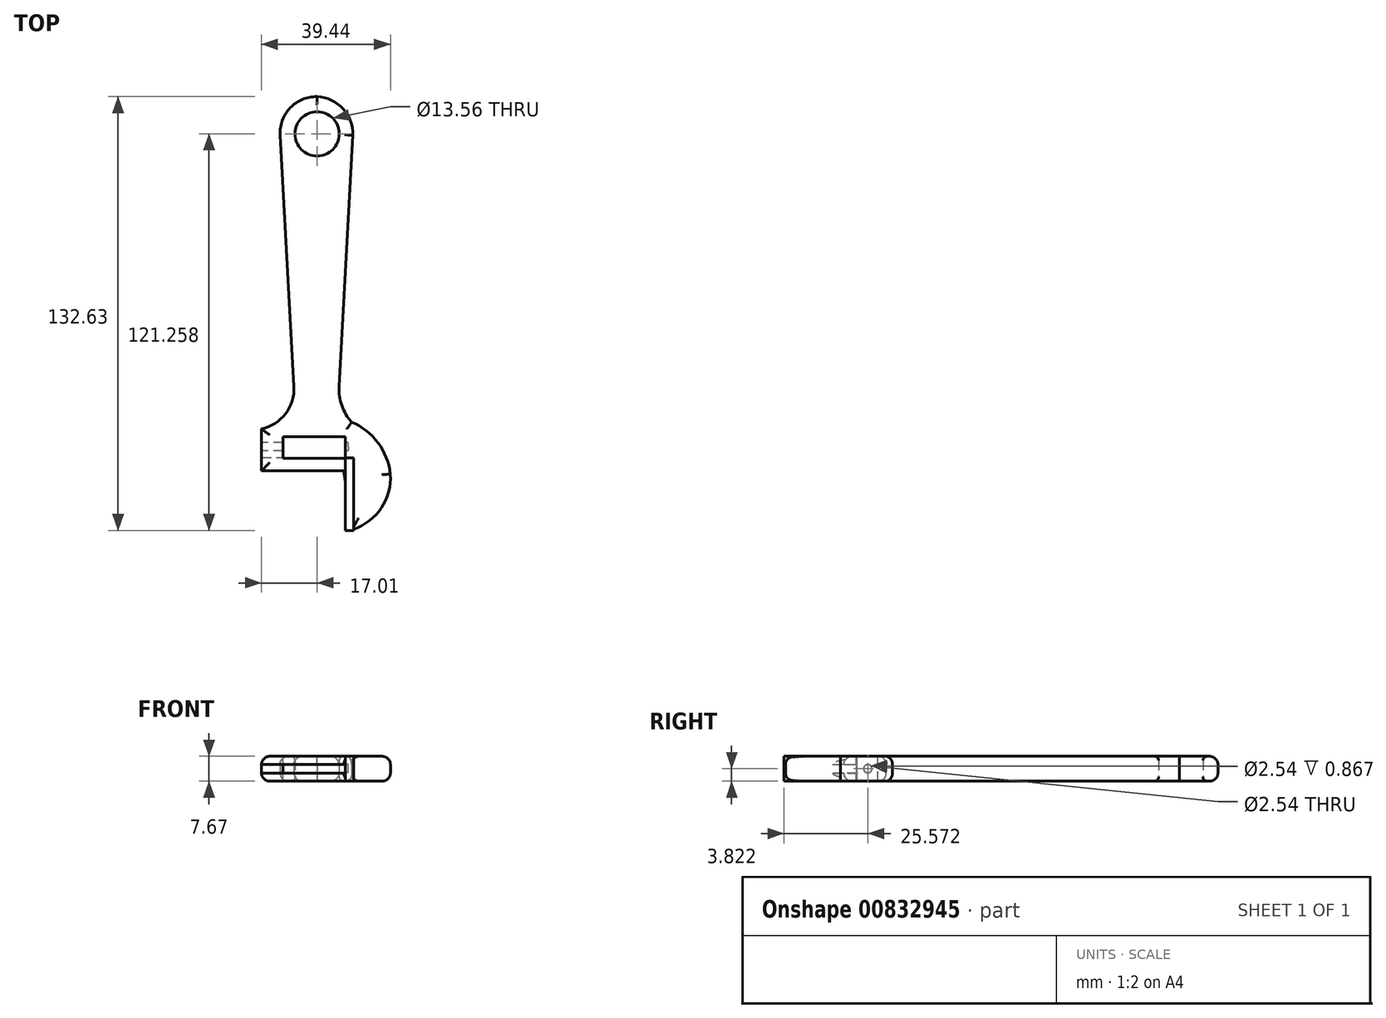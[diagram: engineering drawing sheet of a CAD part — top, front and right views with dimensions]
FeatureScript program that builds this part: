
annotation { "Feature Type Name" : "Feature", "Feature Type Description" : "" }
export const myFeature = defineFeature(function(context is Context, id is Id, definition is map)
    precondition{}
    {
        {
            var Q0;
            Q0=qCreatedBy(makeId("Top.planeOp"),FACE);
            var sketch = newSketch(context, id + "F0", { "sketchPlane" : qUnion([Q0])});
            skLineSegment(sketch, "E0", {"start": v(-7.08, -20.7) * mm, "end": v(-11.31, 56.2) * mm});
            skArc(sketch, "E1", {"start": v(0, 67.96) * mm, "mid": v(-8.22, 64.54) * mm, "end": v(-11.31, 56.2) * mm});
            skArc(sketch, "E2", {"start": v(10.94, 56.2) * mm, "mid": v(7.89, 64.32) * mm, "end": v(0, 67.96) * mm});
            skLineSegment(sketch, "E3", {"start": v(10.94, 56.2) * mm, "end": v(6.71, -20.7) * mm});
            skArc(sketch, "E4", {"start": v(6.71, -20.7) * mm, "mid": v(7.55, -26.5) * mm, "end": v(10.58, -31.54) * mm});
            skArc(sketch, "E5", {"start": v(22.39, -47.4) * mm, "mid": v(18.64, -37.87) * mm, "end": v(10.58, -31.54) * mm});
            skArc(sketch, "E6", {"start": v(10.58, -64.47) * mm, "mid": v(19.5, -58.03) * mm, "end": v(22.39, -47.4) * mm});
            skLineSegment(sketch, "E7", {"start": v(10.58, -64.47) * mm, "end": v(8.18, -46.44) * mm});
            skLineSegment(sketch, "E8", {"start": v(8.18, -46.44) * mm, "end": v(-17.01, -46.44) * mm});
            skLineSegment(sketch, "E9", {"start": v(-17.01, -46.44) * mm, "end": v(-17.01, -33.57) * mm});
            skArc(sketch, "E10", {"start": v(-17.01, -33.57) * mm, "mid": v(-9.65, -28.98) * mm, "end": v(-7.08, -20.7) * mm});
            skSolve(sketch);
        }
        {
            var Q0;
            Q0=makeQuery(id+"F0.imprint","IMPRINT",FACE,{"disambiguationData":[TD([[makeQuery(id+"F0.imprint","IMPRINT",EDGE,{"derivedFrom":sQuery(id+"F0.wireOp",EDGE,"E0")}),-1.0]])]});
            extrude(context, id + "F1", {"entities" : qUnion([Q0]), "depth" : 7.62 * mm, "offsetDistance" : 25.4 * mm});
        }
        {
            var Q0;
            Q0=makeQuery(id+"F1.opExtrude","CAP_FACE",FACE,{"disambiguationData":[OSD([sQuery(id+"F0.wireOp",EDGE,"E0"),sQuery(id+"F0.wireOp",EDGE,"E1"),sQuery(id+"F0.wireOp",EDGE,"E2"),sQuery(id+"F0.wireOp",EDGE,"E3"),sQuery(id+"F0.wireOp",EDGE,"E4"),sQuery(id+"F0.wireOp",EDGE,"E5"),sQuery(id+"F0.wireOp",EDGE,"E6"),sQuery(id+"F0.wireOp",EDGE,"E7"),sQuery(id+"F0.wireOp",EDGE,"E8"),sQuery(id+"F0.wireOp",EDGE,"E9"),sQuery(id+"F0.wireOp",EDGE,"E10")])],"isStart":true});
            fillet(context, id + "F2", {"entities" : qUnion([Q0]), "radius" : 2.54 * mm, "tangentPropagation" : true, "allowEdgeOverflow" : false});
        }
        {
            var Q0;
            Q0=makeQuery(id+"F1.opExtrude","CAP_FACE",FACE,{"disambiguationData":[OSD([sQuery(id+"F0.wireOp",EDGE,"E0"),sQuery(id+"F0.wireOp",EDGE,"E1"),sQuery(id+"F0.wireOp",EDGE,"E2"),sQuery(id+"F0.wireOp",EDGE,"E3"),sQuery(id+"F0.wireOp",EDGE,"E4"),sQuery(id+"F0.wireOp",EDGE,"E5"),sQuery(id+"F0.wireOp",EDGE,"E6"),sQuery(id+"F0.wireOp",EDGE,"E7"),sQuery(id+"F0.wireOp",EDGE,"E8"),sQuery(id+"F0.wireOp",EDGE,"E9"),sQuery(id+"F0.wireOp",EDGE,"E10")])],"isStart":false});
            fillet(context, id + "F3", {"entities" : qUnion([Q0]), "radius" : 2.54 * mm, "tangentPropagation" : true, "allowEdgeOverflow" : false});
        }
        {
            var Q0;
            Q0=qCreatedBy(makeId("Top.planeOp"),FACE);
            var sketch = newSketch(context, id + "F4", { "sketchPlane" : qUnion([Q0])});
            skLineSegment(sketch, "E11.bottom", {"start": v(-10.37, -35.97) * mm, "end": v(8.66, -35.97) * mm});
            skLineSegment(sketch, "E11.top", {"start": v(-10.37, -42.57) * mm, "end": v(8.66, -42.57) * mm});
            skLineSegment(sketch, "E11.left", {"start": v(-10.37, -35.97) * mm, "end": v(-10.37, -42.57) * mm});
            skLineSegment(sketch, "E11.right", {"start": v(8.66, -35.97) * mm, "end": v(8.66, -42.57) * mm});
            skSolve(sketch);
        }
        {
            var Q0;
            Q0 = qSketchRegion(id + "F4", true);
            extrude(context, id + "F5", {"entities" : qUnion([Q0]), "operationType" : NewBodyOperationType.REMOVE, "endBound" : BoundingType.SYMMETRIC, "oppositeDirection" : true, "depth" : 25.4 * mm, "offsetDistance" : 25.4 * mm});
        }
        {
            var Q0;
            Q0=qCreatedBy(makeId("Front.planeOp"),FACE);
            cPlane(context, id + "F6", {"entities" : qUnion([Q0]), "cplaneType" : CPlaneType.OFFSET, "offset" : 42.42 * mm, "width" : 152.4 * mm, "height" : 152.4 * mm});
        }
        {
            var Q0;
            Q0=qCreatedBy(id+"F6.planeOp",FACE);
            var sketch = newSketch(context, id + "F7", { "sketchPlane" : qUnion([Q0])});
            skLineSegment(sketch, "E12.bottom", {"start": v(-17.51, 5.16) * mm, "end": v(8.81, 5.16) * mm});
            skLineSegment(sketch, "E12.top", {"start": v(-17.51, 2.45) * mm, "end": v(8.81, 2.45) * mm});
            skLineSegment(sketch, "E12.left", {"start": v(-17.51, 5.16) * mm, "end": v(-17.51, 2.45) * mm});
            skLineSegment(sketch, "E12.right", {"start": v(8.81, 5.16) * mm, "end": v(8.81, 2.45) * mm});
            skSolve(sketch);
        }
        {
            var Q0;
            Q0 = qSketchRegion(id + "F7", true);
            extrude(context, id + "F8", {"entities" : qUnion([Q0]), "operationType" : NewBodyOperationType.REMOVE, "depth" : 25.4 * mm, "offsetDistance" : 25.4 * mm});
        }
        {
            var Q0;
            Q0=qCreatedBy(makeId("Right.planeOp"),FACE);
            cPlane(context, id + "F9", {"entities" : qUnion([Q0]), "cplaneType" : CPlaneType.OFFSET, "offset" : 12.7 * mm, "oppositeDirection" : true, "width" : 152.4 * mm, "height" : 152.4 * mm});
        }
        {
            var Q0;
            Q0=qCreatedBy(id+"F9.planeOp",FACE);
            var sketch = newSketch(context, id + "F10", { "sketchPlane" : qUnion([Q0])});
            skCircle(sketch, "E13", {"center": v(-39.1, 3.82) * mm, "radius": 1.27 * mm});
            skLineSegment(sketch, "E14", {"start": v(-39.1, 3.82) * mm, "end": v(-39.1, 5.1) * mm});
            skSolve(sketch);
        }
        {
            var Q0;
            Q0 = qSketchRegion(id + "F10", true);
            extrude(context, id + "F11", {"entities" : qUnion([Q0]), "operationType" : NewBodyOperationType.REMOVE, "endBound" : BoundingType.SYMMETRIC, "depth" : 44.45 * mm, "offsetDistance" : 25.4 * mm});
        }
        {
            var Q0;
            Q0=qCreatedBy(makeId("Right.planeOp"),FACE);
            cPlane(context, id + "F12", {"entities" : qUnion([Q0]), "cplaneType" : CPlaneType.OFFSET, "offset" : 8.64 * mm, "width" : 152.4 * mm, "height" : 152.4 * mm});
        }
        {
            var Q0;
            Q0=qCreatedBy(id+"F12.planeOp",FACE);
            var sketch = newSketch(context, id + "F13", { "sketchPlane" : qUnion([Q0])});
            skLineSegment(sketch, "E15.bottom", {"start": v(-42.5, 7.67) * mm, "end": v(-64.67, 7.67) * mm});
            skLineSegment(sketch, "E15.top", {"start": v(-42.5, 0) * mm, "end": v(-64.67, 0) * mm});
            skLineSegment(sketch, "E15.left", {"start": v(-42.5, 7.67) * mm, "end": v(-42.5, 0) * mm});
            skLineSegment(sketch, "E15.right", {"start": v(-64.67, 7.67) * mm, "end": v(-64.67, 0) * mm});
            skSolve(sketch);
        }
        {
            var Q0;
            Q0 = qSketchRegion(id + "F13", true);
            extrude(context, id + "F14", {"entities" : qUnion([Q0]), "operationType" : NewBodyOperationType.ADD, "depth" : 2.54 * mm, "offsetDistance" : 25.4 * mm});
        }
        {
            var Q0;
            Q0=qCreatedBy(makeId("Top.planeOp"),FACE);
            var sketch = newSketch(context, id + "F15", { "sketchPlane" : qUnion([Q0])});
            skCircle(sketch, "E16", {"center": v(0, 56.59) * mm, "radius": 6.78 * mm});
            skSolve(sketch);
        }
        {
            var Q0;
            Q0 = qSketchRegion(id + "F15", true);
            extrude(context, id + "F16", {"entities" : qUnion([Q0]), "operationType" : NewBodyOperationType.REMOVE, "endBound" : BoundingType.SYMMETRIC, "depth" : 25.4 * mm, "offsetDistance" : 25.4 * mm});
        }
        {
            var Q0;
            Q0=makeQuery(id+"F16.boolean.opBoolean","INTERSECT",EDGE,{"derivedFrom":[makeQuery(id+"F1.opExtrude","CAP_FACE",FACE,{"disambiguationData":[OSD([sQuery(id+"F0.wireOp",EDGE,"E0"),sQuery(id+"F0.wireOp",EDGE,"E1"),sQuery(id+"F0.wireOp",EDGE,"E2"),sQuery(id+"F0.wireOp",EDGE,"E3"),sQuery(id+"F0.wireOp",EDGE,"E4"),sQuery(id+"F0.wireOp",EDGE,"E5"),sQuery(id+"F0.wireOp",EDGE,"E6"),sQuery(id+"F0.wireOp",EDGE,"E7"),sQuery(id+"F0.wireOp",EDGE,"E8"),sQuery(id+"F0.wireOp",EDGE,"E9"),sQuery(id+"F0.wireOp",EDGE,"E10")])],"isStart":false}),makeQuery(id+"F16.opExtrude","SWEPT_FACE",FACE,{"disambiguationData":[OSD([sQuery(id+"F15.wireOp",EDGE,"E16")])]})]});
            var Q1;
            Q1=makeQuery(id+"F16.boolean.opBoolean","INTERSECT",EDGE,{"derivedFrom":[makeQuery(id+"F14.boolean.opBoolean","MERGE",FACE,{"derivedFrom":[makeQuery(id+"F1.opExtrude","CAP_FACE",FACE,{"disambiguationData":[OSD([sQuery(id+"F0.wireOp",EDGE,"E0"),sQuery(id+"F0.wireOp",EDGE,"E1"),sQuery(id+"F0.wireOp",EDGE,"E2"),sQuery(id+"F0.wireOp",EDGE,"E3"),sQuery(id+"F0.wireOp",EDGE,"E4"),sQuery(id+"F0.wireOp",EDGE,"E5"),sQuery(id+"F0.wireOp",EDGE,"E6"),sQuery(id+"F0.wireOp",EDGE,"E7"),sQuery(id+"F0.wireOp",EDGE,"E8"),sQuery(id+"F0.wireOp",EDGE,"E9"),sQuery(id+"F0.wireOp",EDGE,"E10")])],"isStart":true}),makeQuery(id+"F14.opExtrude","SWEPT_FACE",FACE,{"disambiguationData":[OSD([sQuery(id+"F13.wireOp",EDGE,"E15.top")])]})]}),makeQuery(id+"F16.opExtrude","SWEPT_FACE",FACE,{"disambiguationData":[OSD([sQuery(id+"F15.wireOp",EDGE,"E16")])]})]});
            fillet(context, id + "F17", {"entities" : qUnion([Q0, Q1]), "radius" : 1.27 * mm, "tangentPropagation" : true, "allowEdgeOverflow" : false});
        }
    });
